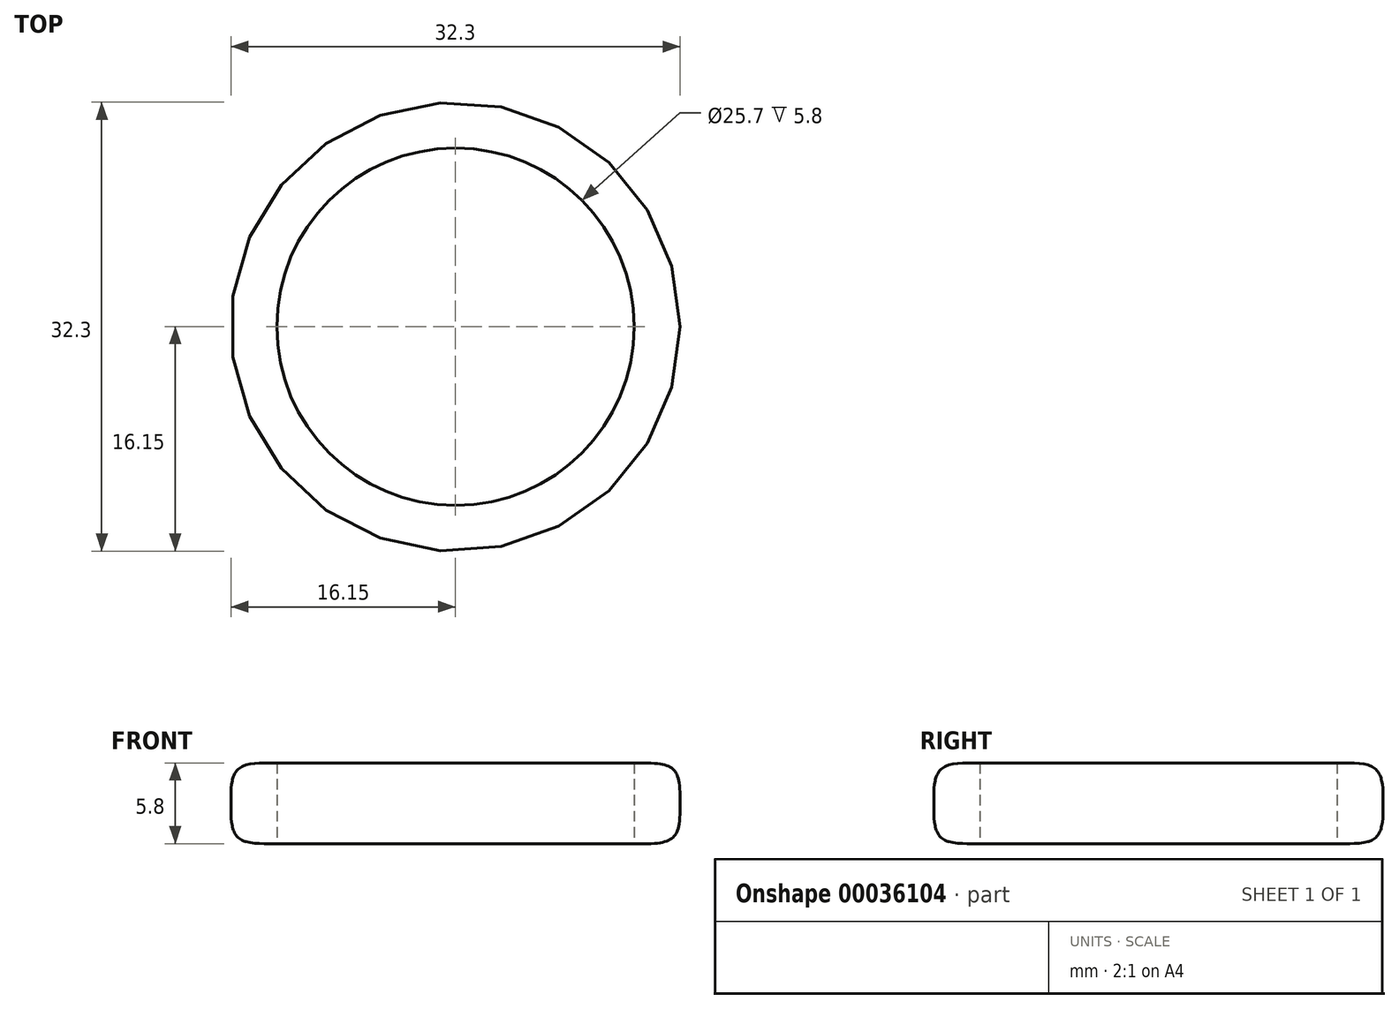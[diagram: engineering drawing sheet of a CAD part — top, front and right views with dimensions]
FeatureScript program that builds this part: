
annotation { "Feature Type Name" : "Feature", "Feature Type Description" : "" }
export const myFeature = defineFeature(function(context is Context, id is Id, definition is map)
    precondition{}
    {
        {
            var Q0;
            Q0=qCreatedBy(makeId("Top.planeOp"),FACE);
            var sketch = newSketch(context, id + "F0", { "sketchPlane" : qUnion([Q0])});
            skCircle(sketch, "E0", {"center": v(0, 0) * mm, "radius": 16.15 * mm});
            skCircle(sketch, "E1", {"center": v(0, 0) * mm, "radius": 12.85 * mm});
            skSolve(sketch);
        }
        {
            var Q0;
            Q0=makeQuery(id+"F0.imprint","IMPRINT",FACE,{"disambiguationData":[TD([[makeQuery(id+"F0.imprint","IMPRINT",EDGE,{"derivedFrom":sQuery(id+"F0.wireOp",EDGE,"E0")}),1.0]])]});
            extrude(context, id + "F1", {"entities" : qUnion([Q0]), "depth" : 5.8 * mm});
        }
        {
            var Q0;
            Q0=makeQuery(id+"F1.opExtrude","SWEPT_FACE",FACE,{"disambiguationData":[OSD([sQuery(id+"F0.wireOp",EDGE,"E0")])]});
            fillet(context, id + "F2", {"entities" : qUnion([Q0]), "radius" : 2.4 * mm, "tangentPropagation" : true, "rho" : 0.6, "crossSection" : FilletCrossSection.CONIC, "allowEdgeOverflow" : false});
        }
    });
